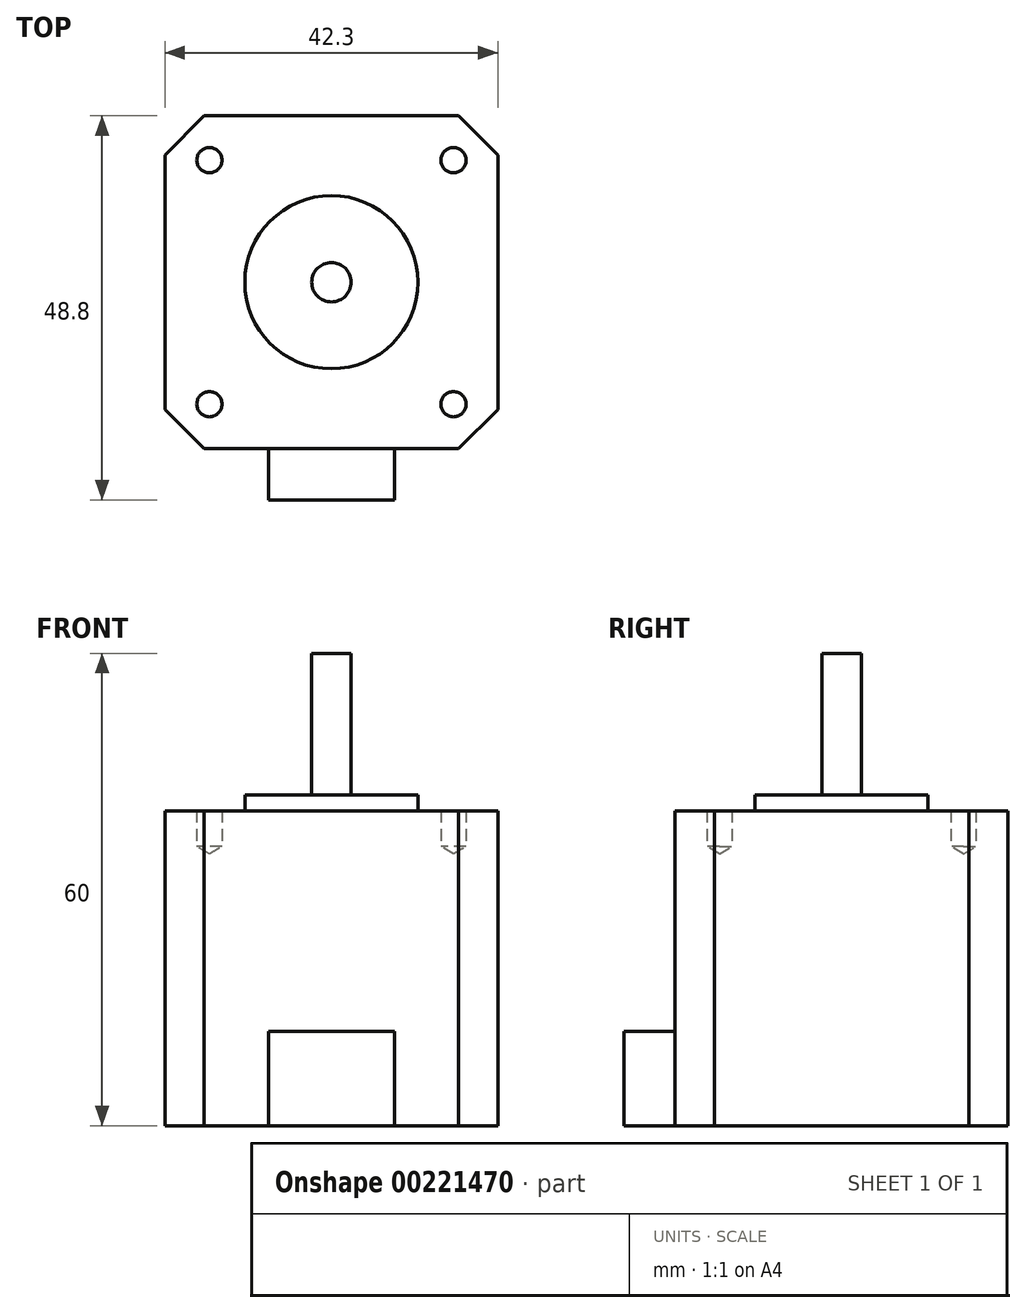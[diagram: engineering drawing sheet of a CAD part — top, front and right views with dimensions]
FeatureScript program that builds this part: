
annotation { "Feature Type Name" : "Feature", "Feature Type Description" : "" }
export const myFeature = defineFeature(function(context is Context, id is Id, definition is map)
    precondition{}
    {
        {
            var Q0;
            Q0=qCreatedBy(makeId("Top.planeOp"),FACE);
            var sketch = newSketch(context, id + "F0", { "sketchPlane" : qUnion([Q0])});
            skLineSegment(sketch, "E0.bottom", {"start": v(0, 0) * mm, "end": v(42.3, 0) * mm});
            skLineSegment(sketch, "E0.top", {"start": v(0, 42.3) * mm, "end": v(42.3, 42.3) * mm});
            skLineSegment(sketch, "E0.left", {"start": v(0, 0) * mm, "end": v(0, 42.3) * mm});
            skLineSegment(sketch, "E0.right", {"start": v(42.3, 0) * mm, "end": v(42.3, 42.3) * mm});
            skSolve(sketch);
        }
        {
            var Q0;
            Q0=makeQuery(id+"F0.imprint","IMPRINT",FACE,{"disambiguationData":[TD([[makeQuery(id+"F0.imprint","IMPRINT",EDGE,{"derivedFrom":sQuery(id+"F0.wireOp",EDGE,"E0.bottom")}),1.0]])]});
            var Q1;
            Q1=sQuery(id+"F0.wireOp",EDGE,"E0.top");
            extrude(context, id + "F1", {"entities" : qUnion([Q0]), "surfaceEntities" : qUnion([Q1]), "depth" : 40 * mm});
        }
        {
            var Q0;
            Q0=makeQuery(id+"F1.opExtrude","CAP_FACE",FACE,{"disambiguationData":[OSD([sQuery(id+"F0.wireOp",EDGE,"E0.bottom"),sQuery(id+"F0.wireOp",EDGE,"E0.top"),sQuery(id+"F0.wireOp",EDGE,"E0.left"),sQuery(id+"F0.wireOp",EDGE,"E0.right")])],"isStart":false});
            var sketch = newSketch(context, id + "F2", { "sketchPlane" : qUnion([Q0])});
            skLineSegment(sketch, "E1.bottom", {"start": v(5.65, 36.65) * mm, "end": v(36.65, 36.65) * mm, "construction": true});
            skLineSegment(sketch, "E1.top", {"start": v(5.65, 5.65) * mm, "end": v(36.65, 5.65) * mm, "construction": true});
            skLineSegment(sketch, "E1.left", {"start": v(5.65, 36.65) * mm, "end": v(5.65, 5.65) * mm, "construction": true});
            skLineSegment(sketch, "E1.right", {"start": v(36.65, 36.65) * mm, "end": v(36.65, 5.65) * mm, "construction": true});
            skPoint(sketch, "E2", {"position": v(21.15, 42.3) * mm});
            skPoint(sketch, "E3", {"position": v(21.15, 36.65) * mm});
            skPoint(sketch, "E4", {"position": v(36.65, 21.15) * mm});
            skPoint(sketch, "E5", {"position": v(42.3, 21.15) * mm});
            skSolve(sketch);
        }
        {
            var Q0;
            Q0=sQuery(id+"F2.wireOp",VERTEX,"E1.left.start");
            var Q1;
            Q1=sQuery(id+"F2.wireOp",VERTEX,"E1.right.start");
            var Q2;
            Q2=sQuery(id+"F2.wireOp",VERTEX,"E1.left.end");
            var Q3;
            Q3=sQuery(id+"F2.wireOp",VERTEX,"E1.top.end");
            var Q4;
            Q4=makeQuery(id+"F1.opExtrude","SWEPT_BODY",BODY,{"disambiguationData":[OSD([sQuery(id+"F0.wireOp",EDGE,"E0.bottom"),sQuery(id+"F0.wireOp",EDGE,"E0.top"),sQuery(id+"F0.wireOp",EDGE,"E0.left"),sQuery(id+"F0.wireOp",EDGE,"E0.right")])]});
            hole(context, id + "F3", {"style" : HoleStyle.SIMPLE, "endStyle" : HoleEndStyle.BLIND, "standardTappedOrClearance" : lookupTablePath({ "standard" : "ISO", "size" : "3.2", "type" : "Drilled" }), "standardBlindInLast" : lookupTablePath({ "standard" : "ISO", "size" : "3.2", "type" : "Drilled" }), "holeDiameter" : 3.2 * mm, "holeDepth" : 4.5 * mm, "locations" : qUnion([Q0, Q1, Q2, Q3]), "scope" : qUnion([Q4])});
        }
        {
            var Q0;
            Q0=makeQuery(id+"F1.opExtrude","CAP_FACE",FACE,{"disambiguationData":[OSD([sQuery(id+"F0.wireOp",EDGE,"E0.bottom"),sQuery(id+"F0.wireOp",EDGE,"E0.top"),sQuery(id+"F0.wireOp",EDGE,"E0.left"),sQuery(id+"F0.wireOp",EDGE,"E0.right")])],"isStart":false});
            var sketch = newSketch(context, id + "F4", { "sketchPlane" : qUnion([Q0])});
            skCircle(sketch, "E6", {"center": v(21.15, 21.15) * mm, "radius": 11 * mm});
            skPoint(sketch, "E6.centerSnap0", {"position": v(42.3, 21.15) * mm});
            skPoint(sketch, "E6.centerSnap1", {"position": v(21.15, 42.3) * mm});
            skSolve(sketch);
        }
        {
            var Q0;
            Q0=makeQuery(id+"F4.imprint","IMPRINT",FACE,{"disambiguationData":[TD([[makeQuery(id+"F4.imprint","IMPRINT",EDGE,{"derivedFrom":sQuery(id+"F4.wireOp",EDGE,"E6")}),1.0]])]});
            extrude(context, id + "F5", {"entities" : qUnion([Q0]), "operationType" : NewBodyOperationType.ADD, "depth" : 2 * mm});
        }
        {
            var Q0;
            Q0=makeQuery(id+"F5.opExtrude","CAP_FACE",FACE,{"disambiguationData":[OSD([sQuery(id+"F4.wireOp",EDGE,"E6")])],"isStart":false});
            var sketch = newSketch(context, id + "F6", { "sketchPlane" : qUnion([Q0])});
            skCircle(sketch, "E7", {"center": v(21.15, 21.15) * mm, "radius": 2.5 * mm});
            skSolve(sketch);
        }
        {
            var Q0;
            Q0=makeQuery(id+"F6.imprint","IMPRINT",FACE,{"disambiguationData":[TD([[makeQuery(id+"F6.imprint","IMPRINT",EDGE,{"derivedFrom":sQuery(id+"F6.wireOp",EDGE,"E7")}),1.0]])]});
            extrude(context, id + "F7", {"entities" : qUnion([Q0]), "operationType" : NewBodyOperationType.ADD, "depth" : 18 * mm});
        }
        {
            var Q0;
            Q0=makeQuery(id+"F1.opExtrude","SWEPT_EDGE",EDGE,{"disambiguationData":[OSD([sQuery(id+"F0.wireOp",EDGE,"E0.top"),sQuery(id+"F0.wireOp",EDGE,"E0.right")])]});
            var Q1;
            Q1=makeQuery(id+"F1.opExtrude","SWEPT_EDGE",EDGE,{"disambiguationData":[OSD([sQuery(id+"F0.wireOp",EDGE,"E0.bottom"),sQuery(id+"F0.wireOp",EDGE,"E0.right")])]});
            var Q2;
            Q2=makeQuery(id+"F1.opExtrude","SWEPT_EDGE",EDGE,{"disambiguationData":[OSD([sQuery(id+"F0.wireOp",EDGE,"E0.top"),sQuery(id+"F0.wireOp",EDGE,"E0.left")])]});
            var Q3;
            Q3=makeQuery(id+"F1.opExtrude","SWEPT_EDGE",EDGE,{"disambiguationData":[OSD([sQuery(id+"F0.wireOp",EDGE,"E0.bottom"),sQuery(id+"F0.wireOp",EDGE,"E0.left")])]});
            chamfer(context, id + "F8", {"entities" : qUnion([Q0, Q1, Q2, Q3]), "width" : 5 * mm, "tangentPropagation" : true});
        }
        {
            var Q0;
            Q0=makeQuery(id+"F1.opExtrude","SWEPT_FACE",FACE,{"disambiguationData":[OSD([sQuery(id+"F0.wireOp",EDGE,"E0.bottom")])]});
            var sketch = newSketch(context, id + "F9", { "sketchPlane" : qUnion([Q0])});
            skLineSegment(sketch, "E8.bottom", {"start": v(13.15, 0) * mm, "end": v(29.15, 0) * mm});
            skLineSegment(sketch, "E8.top", {"start": v(13.15, 12) * mm, "end": v(29.15, 12) * mm});
            skLineSegment(sketch, "E8.left", {"start": v(13.15, 0) * mm, "end": v(13.15, 12) * mm});
            skLineSegment(sketch, "E8.right", {"start": v(29.15, 0) * mm, "end": v(29.15, 12) * mm});
            skPoint(sketch, "E9", {"position": v(21.15, 0) * mm});
            skSolve(sketch);
        }
        {
            var Q0;
            Q0=makeQuery(id+"F9.imprint","IMPRINT",FACE,{"disambiguationData":[TD([[makeQuery(id+"F9.imprint","IMPRINT",EDGE,{"derivedFrom":sQuery(id+"F9.wireOp",EDGE,"E8.bottom")}),1.0]])]});
            extrude(context, id + "F10", {"entities" : qUnion([Q0]), "operationType" : NewBodyOperationType.ADD, "depth" : 6.5 * mm});
        }
    });
